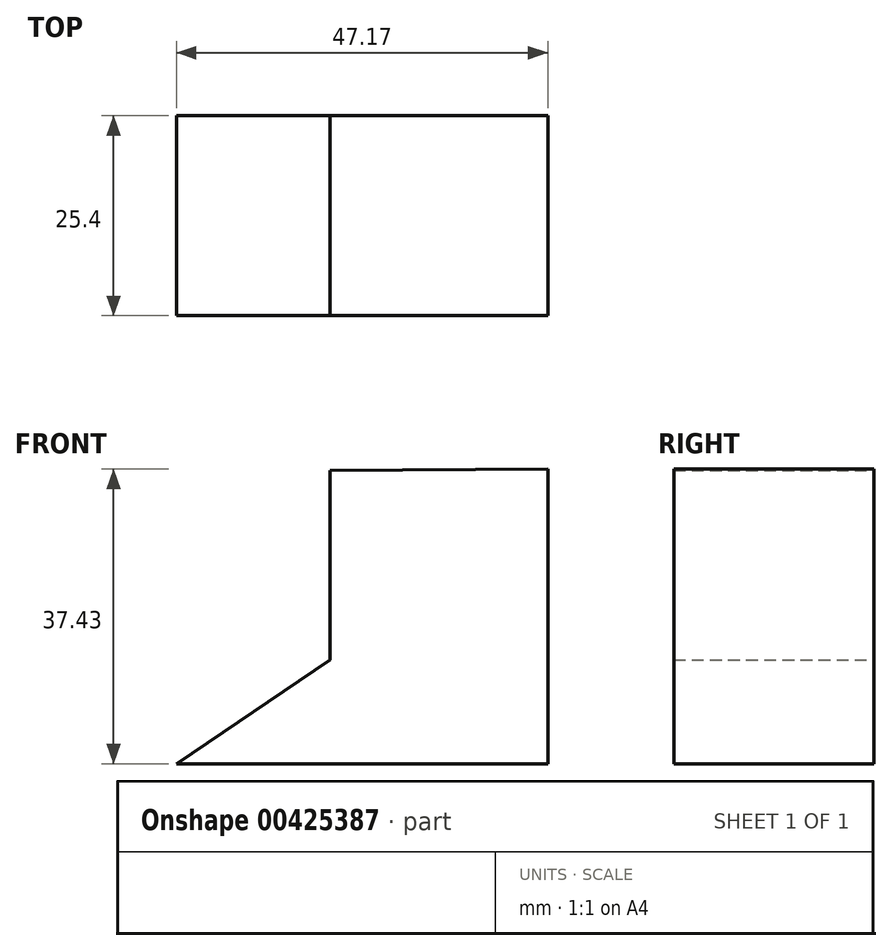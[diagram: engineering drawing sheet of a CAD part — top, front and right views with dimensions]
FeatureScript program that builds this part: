
annotation { "Feature Type Name" : "Feature", "Feature Type Description" : "" }
export const myFeature = defineFeature(function(context is Context, id is Id, definition is map)
    precondition{}
    {
        {
            var Q0;
            Q0=qCreatedBy(makeId("Front.planeOp"),FACE);
            var sketch = newSketch(context, id + "F0", { "sketchPlane" : qUnion([Q0])});
            skLineSegment(sketch, "E0", {"start": v(0, 37.43) * mm, "end": v(0, 0) * mm});
            skLineSegment(sketch, "E1", {"start": v(0, 0) * mm, "end": v(-47.17, 0) * mm});
            skLineSegment(sketch, "E2", {"start": v(-47.17, 0) * mm, "end": v(-27.69, 13.18) * mm});
            skLineSegment(sketch, "E3", {"start": v(-27.69, 13.18) * mm, "end": v(-27.69, 37.24) * mm});
            skLineSegment(sketch, "E4", {"start": v(-27.69, 37.24) * mm, "end": v(0, 37.43) * mm});
            skSolve(sketch);
        }
        {
            var Q0;
            Q0=makeQuery(id+"F0.imprint","IMPRINT",FACE,{"disambiguationData":[TD([[makeQuery(id+"F0.imprint","IMPRINT",EDGE,{"derivedFrom":sQuery(id+"F0.wireOp",EDGE,"E0")}),-1.0]])]});
            extrude(context, id + "F1", {"entities" : qUnion([Q0]), "depth" : 25.4 * mm});
        }
    });
